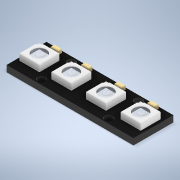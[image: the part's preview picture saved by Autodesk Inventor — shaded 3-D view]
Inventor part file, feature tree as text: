
AUTODESK INVENTOR PART (.ipt)
format: ipt  version: 2020.1 (Build 241239000, 239)  size: 255,488 bytes
history: native  units: mm
features: projected_geometry x7, extrude x6, sketch x3, plane x1
ambient origin geometry x8: Origin, YZ Plane, XZ Plane, XY Plane, X Axis, Y Axis, Z Axis, Center Point
bodies: Solid1 (feature_tree)
feature tree (17):
  sketch  "Sketch1"  dims[d0=31.84mm d1=10.0mm]
  extrude  "Extrusion1"  Depth=10.0mm
  extrude  "Extrusion2"  Depth=1.0mm
  extrude  "Extrusion3"  Depth=7.5mm
  sketch  "Sketch2"  dims[d2=1.85mm d3=1.0mm]
  extrude  "Extrusion4"  Depth=2.0mm
  extrude  "Extrusion5"  Depth=3.2mm
  plane  "Work Plane1"
  extrude  "Extrusion7"  Depth=0.5mm
  projected_geometry  "Projected Loop1"
  projected_geometry  "Projected Loop2"
  projected_geometry  "Projected Loop3"
  projected_geometry  "Projected Loop4"
  sketch  "Sketch3"  dims[d4=7.5mm d5=7.5mm d6=2.0mm d7=3.2mm d8=0.5mm d9=5.0mm d10=0.7mm d11=3.7mm d12=0.7mm d14=6.45mm d15=6.45mm d16=2.5mm d18=3.7mm d19=1.6mm d20=0.0mm d21=1.6mm d22=0.0mm d23=0.9mm d24=0.0mm d25=3.5mm d26=45.0deg d27=1.0mm d28=0.2mm d29=0.0mm d30=0.8mm d31=0.0mm d34=-0.1mm d35=10.0mm d36=0.0mm]
  projected_geometry  "Projected Loop5"
  projected_geometry  "Projected Loop6"
  projected_geometry  "Projected Loop7"
